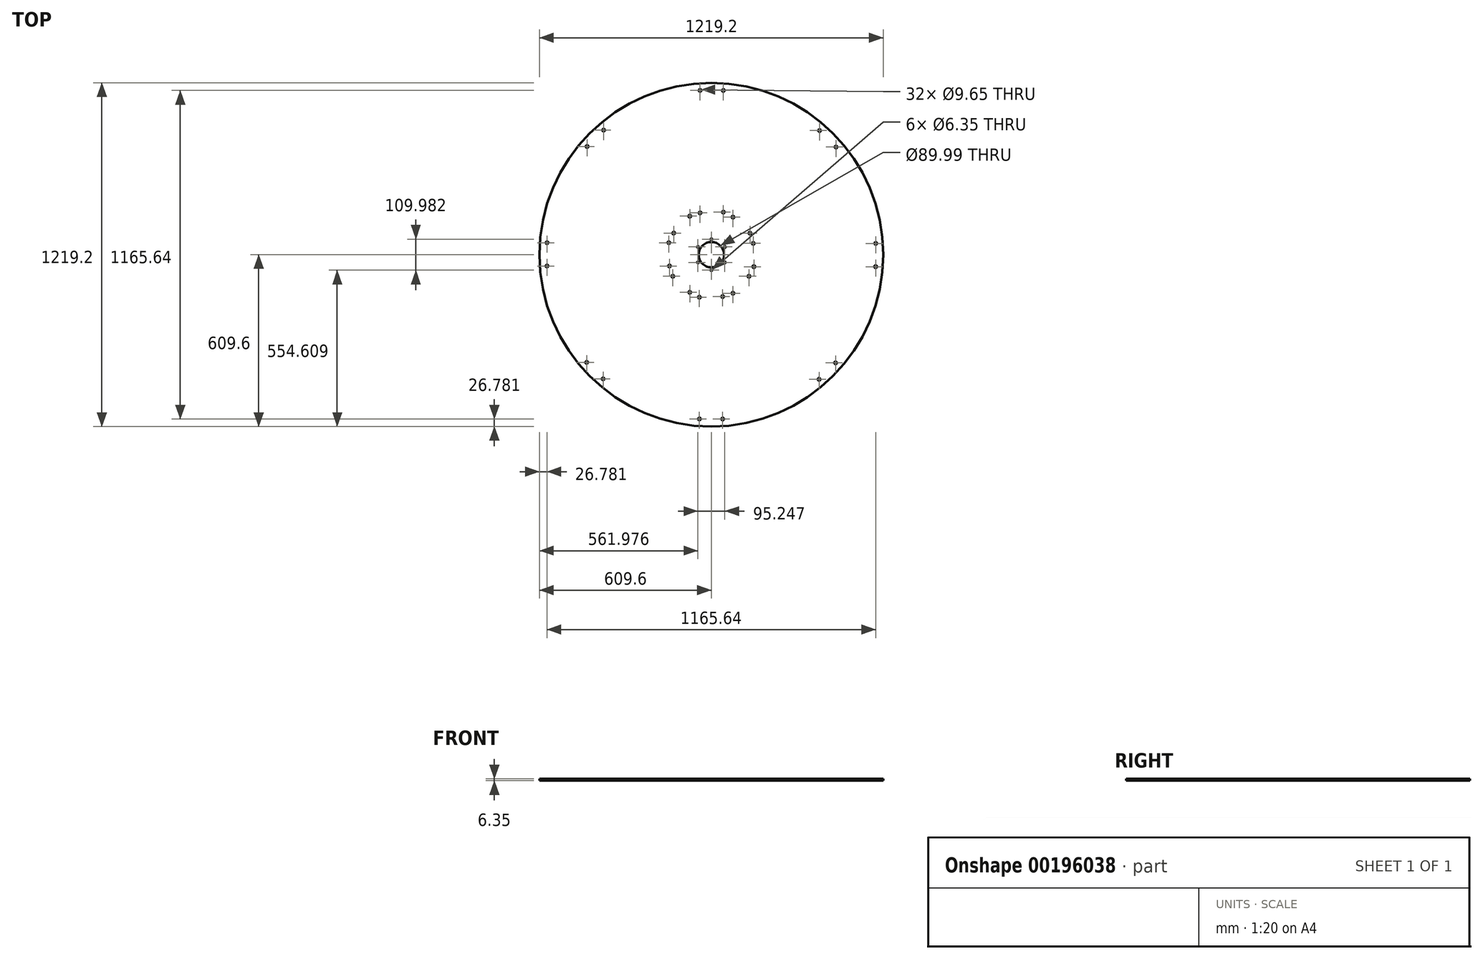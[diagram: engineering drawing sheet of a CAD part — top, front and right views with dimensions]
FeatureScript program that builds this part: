
annotation { "Feature Type Name" : "Feature", "Feature Type Description" : "" }
export const myFeature = defineFeature(function(context is Context, id is Id, definition is map)
    precondition{}
    {
        {
            var Q0;
            Q0=qCreatedBy(makeId("Top.planeOp"),FACE);
            var sketch = newSketch(context, id + "F0", { "sketchPlane" : qUnion([Q0])});
            skCircle(sketch, "E0", {"center": v(0, 0) * mm, "radius": 45 * mm});
            skCircle(sketch, "E1", {"center": v(0, 0) * mm, "radius": 65 * mm, "construction": true});
            skCircle(sketch, "E2", {"center": v(0, 55) * mm, "radius": 3.18 * mm});
            skCircle(sketch, "E3.1.0", {"center": v(-47.62, 27.5) * mm, "radius": 3.18 * mm});
            skCircle(sketch, "E3.2.0", {"center": v(-47.62, -27.5) * mm, "radius": 3.18 * mm});
            skCircle(sketch, "E3.3.0", {"center": v(0, -55) * mm, "radius": 3.18 * mm});
            skCircle(sketch, "E3.4.0", {"center": v(47.62, -27.5) * mm, "radius": 3.18 * mm});
            skCircle(sketch, "E3.5.0", {"center": v(47.62, 27.5) * mm, "radius": 3.18 * mm});
            skCircle(sketch, "E4", {"center": v(0, 0) * mm, "radius": 609.6 * mm});
            skPoint(sketch, "E5.center", {"position": v(0.6, 0) * mm});
            skCircle(sketch, "E6", {"center": v(-40.14, 582.82) * mm, "radius": 4.83 * mm});
            skCircle(sketch, "E7", {"center": v(42.4, 582.66) * mm, "radius": 4.83 * mm});
            skCircle(sketch, "E8.1.0", {"center": v(-440.5, 383.73) * mm, "radius": 4.83 * mm});
            skCircle(sketch, "E8.1.1", {"center": v(-382.02, 441.99) * mm, "radius": 4.83 * mm});
            skCircle(sketch, "E8.2.0", {"center": v(-582.82, -40.14) * mm, "radius": 4.83 * mm});
            skCircle(sketch, "E8.2.1", {"center": v(-582.66, 42.4) * mm, "radius": 4.83 * mm});
            skCircle(sketch, "E8.3.0", {"center": v(-383.73, -440.5) * mm, "radius": 4.83 * mm});
            skCircle(sketch, "E8.3.1", {"center": v(-441.99, -382.02) * mm, "radius": 4.83 * mm});
            skCircle(sketch, "E8.4.0", {"center": v(40.14, -582.82) * mm, "radius": 4.83 * mm});
            skCircle(sketch, "E8.4.1", {"center": v(-42.4, -582.66) * mm, "radius": 4.83 * mm});
            skCircle(sketch, "E8.5.0", {"center": v(440.5, -383.73) * mm, "radius": 4.83 * mm});
            skCircle(sketch, "E8.5.1", {"center": v(382.02, -441.99) * mm, "radius": 4.83 * mm});
            skCircle(sketch, "E8.6.0", {"center": v(582.82, 40.14) * mm, "radius": 4.83 * mm});
            skCircle(sketch, "E8.6.1", {"center": v(582.66, -42.4) * mm, "radius": 4.83 * mm});
            skCircle(sketch, "E8.7.0", {"center": v(383.73, 440.5) * mm, "radius": 4.83 * mm});
            skCircle(sketch, "E8.7.1", {"center": v(441.99, 382.02) * mm, "radius": 4.83 * mm});
            skCircle(sketch, "E9", {"center": v(42.55, 150.86) * mm, "radius": 4.83 * mm});
            skCircle(sketch, "E10", {"center": v(-40.16, 148.45) * mm, "radius": 4.83 * mm});
            skCircle(sketch, "E11.1.0", {"center": v(-133.36, 76.57) * mm, "radius": 4.83 * mm});
            skCircle(sketch, "E11.1.2", {"center": v(-76.59, 136.76) * mm, "radius": 4.83 * mm});
            skCircle(sketch, "E11.2.0", {"center": v(-148.45, -40.16) * mm, "radius": 4.83 * mm});
            skCircle(sketch, "E11.2.2", {"center": v(-150.86, 42.55) * mm, "radius": 4.83 * mm});
            skCircle(sketch, "E11.3.0", {"center": v(-76.57, -133.36) * mm, "radius": 4.83 * mm});
            skCircle(sketch, "E11.3.2", {"center": v(-136.76, -76.59) * mm, "radius": 4.83 * mm});
            skCircle(sketch, "E11.4.0", {"center": v(40.16, -148.45) * mm, "radius": 4.83 * mm});
            skCircle(sketch, "E11.4.2", {"center": v(-42.55, -150.86) * mm, "radius": 4.83 * mm});
            skCircle(sketch, "E11.5.0", {"center": v(133.36, -76.57) * mm, "radius": 4.83 * mm});
            skCircle(sketch, "E11.5.2", {"center": v(76.59, -136.76) * mm, "radius": 4.83 * mm});
            skCircle(sketch, "E11.6.0", {"center": v(148.45, 40.16) * mm, "radius": 4.83 * mm});
            skCircle(sketch, "E11.6.2", {"center": v(150.86, -42.55) * mm, "radius": 4.83 * mm});
            skCircle(sketch, "E11.7.0", {"center": v(76.57, 133.36) * mm, "radius": 4.83 * mm});
            skCircle(sketch, "E11.7.2", {"center": v(136.76, 76.59) * mm, "radius": 4.83 * mm});
            skLineSegment(sketch, "E12", {"start": v(-382.02, 441.99) * mm, "end": v(-76.59, 136.76) * mm, "construction": true});
            skLineSegment(sketch, "E13", {"start": v(-440.5, 383.73) * mm, "end": v(-133.36, 76.57) * mm, "construction": true});
            skLineSegment(sketch, "E14.1.0", {"start": v(-581.69, 41.43) * mm, "end": v(-149.89, 41.57) * mm, "construction": true});
            skLineSegment(sketch, "E14.1.1", {"start": v(-581.85, -41.12) * mm, "end": v(-147.47, -41.13) * mm, "construction": true});
            skLineSegment(sketch, "E14.2.0", {"start": v(-439.64, -382.99) * mm, "end": v(-134.4, -77.56) * mm, "construction": true});
            skLineSegment(sketch, "E14.2.1", {"start": v(-381.38, -441.47) * mm, "end": v(-74.22, -134.34) * mm, "construction": true});
            skLineSegment(sketch, "E14.3.0", {"start": v(-39.08, -582.66) * mm, "end": v(-39.22, -150.86) * mm, "construction": true});
            skLineSegment(sketch, "E14.3.1", {"start": v(43.47, -582.82) * mm, "end": v(43.48, -148.45) * mm, "construction": true});
            skLineSegment(sketch, "E14.4.0", {"start": v(385.34, -440.61) * mm, "end": v(79.91, -135.38) * mm, "construction": true});
            skLineSegment(sketch, "E14.4.1", {"start": v(443.82, -382.35) * mm, "end": v(136.69, -75.2) * mm, "construction": true});
            skLineSegment(sketch, "E14.5.0", {"start": v(585, -40.06) * mm, "end": v(153.2, -40.2) * mm, "construction": true});
            skLineSegment(sketch, "E14.5.1", {"start": v(585.17, 42.5) * mm, "end": v(150.8, 42.5) * mm, "construction": true});
            skLineSegment(sketch, "E14.6.0", {"start": v(442.96, 384.37) * mm, "end": v(137.73, 78.94) * mm, "construction": true});
            skLineSegment(sketch, "E14.6.1", {"start": v(384.7, 442.85) * mm, "end": v(77.55, 135.71) * mm, "construction": true});
            skLineSegment(sketch, "E14.7.0", {"start": v(42.4, 584.04) * mm, "end": v(42.55, 152.24) * mm, "construction": true});
            skLineSegment(sketch, "E14.7.1", {"start": v(-40.14, 584.2) * mm, "end": v(-40.16, 149.82) * mm, "construction": true});
            skPoint(sketch, "E14.center", {"position": v(1.66, 0.69) * mm});
            skSolve(sketch);
        }
        {
            var Q0;
            Q0=makeQuery(id+"F0.imprint","IMPRINT",FACE,{"disambiguationData":[TD([[makeQuery(id+"F0.imprint","IMPRINT",EDGE,{"derivedFrom":sQuery(id+"F0.wireOp",EDGE,"E0")}),-1.0]])]});
            extrude(context, id + "F1", {"entities" : qUnion([Q0]), "depth" : 6.35 * mm});
        }
    });
